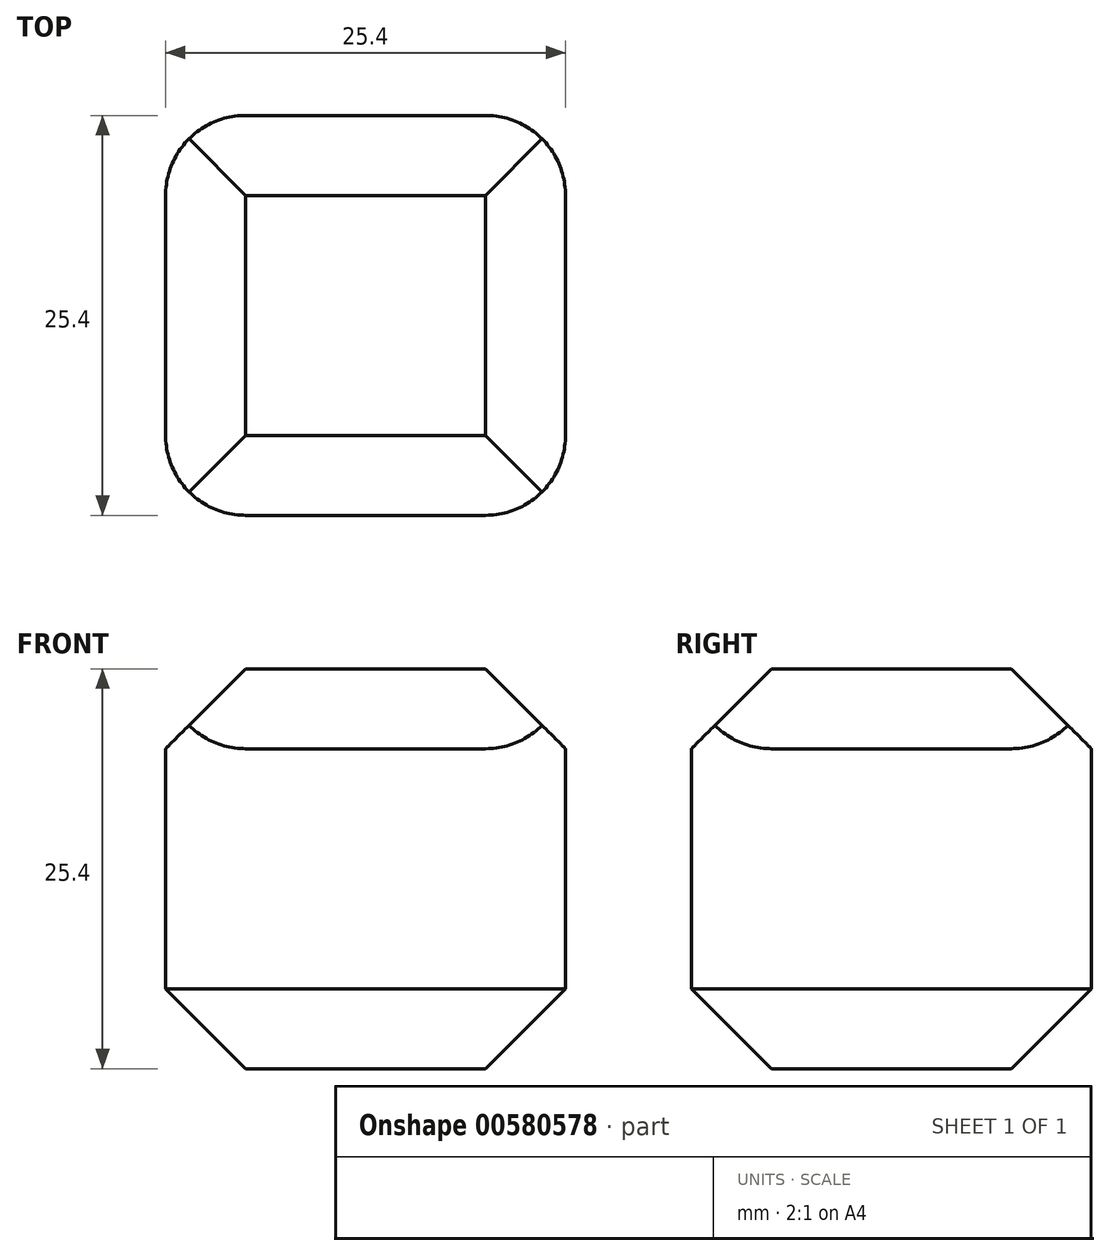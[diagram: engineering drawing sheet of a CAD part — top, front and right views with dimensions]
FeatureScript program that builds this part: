
annotation { "Feature Type Name" : "Feature", "Feature Type Description" : "" }
export const myFeature = defineFeature(function(context is Context, id is Id, definition is map)
    precondition{}
    {
        {
            var Q0;
            Q0=qCreatedBy(makeId("Front.planeOp"),FACE);
            var sketch = newSketch(context, id + "F0", { "sketchPlane" : qUnion([Q0])});
            skLineSegment(sketch, "E0", {"start": v(0, 0) * mm, "end": v(25.4, 0) * mm});
            skLineSegment(sketch, "E1", {"start": v(25.4, 0) * mm, "end": v(25.4, 25.4) * mm});
            skLineSegment(sketch, "E2", {"start": v(25.4, 25.4) * mm, "end": v(0, 25.4) * mm});
            skLineSegment(sketch, "E3", {"start": v(0, 25.4) * mm, "end": v(0, 0) * mm});
            skSolve(sketch);
        }
        {
            var Q0;
            Q0=makeQuery(id+"F0.imprint","IMPRINT",FACE,{"disambiguationData":[TD([[makeQuery(id+"F0.imprint","IMPRINT",EDGE,{"derivedFrom":sQuery(id+"F0.wireOp",EDGE,"E0")}),1.0]])]});
            extrude(context, id + "F1", {"entities" : qUnion([Q0]), "depth" : 25.4 * mm, "offsetDistance" : 25.4 * mm});
        }
        {
            var Q0;
            Q0=makeQuery(id+"F1.opExtrude","SWEPT_EDGE",EDGE,{"disambiguationData":[OSD([sQuery(id+"F0.wireOp",EDGE,"E1"),sQuery(id+"F0.wireOp",EDGE,"E2")])]});
            var Q1;
            Q1=makeQuery(id+"F1.opExtrude","CAP_EDGE",EDGE,{"disambiguationData":[OSD([sQuery(id+"F0.wireOp",EDGE,"E2")])],"isStart":false});
            var Q2;
            Q2=makeQuery(id+"F1.opExtrude","CAP_EDGE",EDGE,{"disambiguationData":[OSD([sQuery(id+"F0.wireOp",EDGE,"E2")])],"isStart":true});
            var Q3;
            Q3=makeQuery(id+"F1.opExtrude","SWEPT_EDGE",EDGE,{"disambiguationData":[OSD([sQuery(id+"F0.wireOp",EDGE,"E2"),sQuery(id+"F0.wireOp",EDGE,"E3")])]});
            chamfer(context, id + "F2", {"entities" : qUnion([Q0, Q1, Q2, Q3]), "width" : 5.08 * mm, "tangentPropagation" : true});
        }
        {
            var Q0;
            Q0=makeQuery(id+"F1.opExtrude","CAP_EDGE",EDGE,{"disambiguationData":[OSD([sQuery(id+"F0.wireOp",EDGE,"E1")])],"isStart":false});
            var Q1;
            Q1=makeQuery(id+"F1.opExtrude","CAP_EDGE",EDGE,{"disambiguationData":[OSD([sQuery(id+"F0.wireOp",EDGE,"E1")])],"isStart":true});
            var Q2;
            Q2=makeQuery(id+"F1.opExtrude","CAP_EDGE",EDGE,{"disambiguationData":[OSD([sQuery(id+"F0.wireOp",EDGE,"E3")])],"isStart":false});
            var Q3;
            Q3=makeQuery(id+"F1.opExtrude","CAP_EDGE",EDGE,{"disambiguationData":[OSD([sQuery(id+"F0.wireOp",EDGE,"E3")])],"isStart":true});
            fillet(context, id + "F3", {"entities" : qUnion([Q0, Q1, Q2, Q3]), "radius" : 5.08 * mm, "tangentPropagation" : true, "allowEdgeOverflow" : false});
        }
        {
            var Q0;
            Q0=makeQuery(id+"F1.opExtrude","CAP_EDGE",EDGE,{"disambiguationData":[OSD([sQuery(id+"F0.wireOp",EDGE,"E0")])],"isStart":false});
            chamfer(context, id + "F4", {"entities" : qUnion([Q0]), "width" : 5.08 * mm, "tangentPropagation" : true});
        }
    });
